# Revit family: Hager-Vega-IP30-syst-NoHosted-FR-fr
name_source: partatom
category: Electrical Equipment
units: mm (PartAtom-declared; Revit-internal decimal feet)

## family parameters
Always vertical = Yes
Cut with Voids When Loaded = No
Panel Configuration = Two Columns, Circuits Across
Part Type = Panelboard
Room Calculation Point = No
Round Connector Dimension = Use Diameter
Shared = No
Work Plane-Based = Yes

## types (8) — shared parameters
Default Elevation = 1219 mm
EF000003 - mode de pose = EV000384 - saillie
EF000007 - couleur = EV000202 - blanc
EF000008 - largeur = 400 mm  [stored 1.31234 ft]
EF000049 - profondeur = 146 mm  [stored 0.479003 ft]
EF000116 - numéro RAL = 9010
EF000118 - avec cadre/support de montage = No
EF000339 - type de capot = EV001012 - couvercle
EF001062 - finition CEM = No
EF001088 - possibilité de montage en saillie = Yes
EF001131 - profondeur intérieure = 120 mm
EF001134 - rail DIN = Yes
EF001596 - matériau du boîtier/corps = EV000139 - plastique
EF002950 - largeur en nombre de modules = 18
EF004462 - type de fermeture = EV000154 - autre
EF005474 - indice de protection (IP) = EV006410 - IP30
EF006244 - couvercle/porte transparent(e) = No
EF006306 - avec serrure = No
EF009212 - finition du couvercle = EV000116 - fermé
EF015776 - borne de mise à la terre = Yes
EF015777 - borne à conducteur neutre = No
EF015941 - porte pour transmission du signal = Yes
HG000001 - nombre de colonnes = 1
HG000002 - avec porte = No
HG000003 - Gamme = Vega
HG000005 - Epaisseur = 3 mm  [stored 0.00984252 ft]
HG000006 - Encastré = No
HG000009 - Porte à double battant = No
HG000010 - Portes asymétriques = No
HG000011 - Rangées du bas vides = No
HG000017 - Distance entre pôles = 18 mm  [stored 0.0590551 ft]
Manufacturer = Hager
Type Comments = Vega
zero-valued in all types: EF000218 - profondeur d'encastrement, EF000332 - hauteur d'encastrement, EF000846 - largeur d'encastrement, HG000007 - Nombre de colonnes vides, HG000008 - Nombre de rangées vides

## per-type parameters (varying)
| type | EF000040 - hauteur | EF000266 - nombre de rangées | HG000004 - Référence fabricant | Model |
| Saillie IP30 L400 H325 P146 18 Modules - VB118A | 325 mm | 1 | VB118A | VB118A |
| Saillie IP30 L400 H325 P146 18 Modules - VB118X | 325 mm | 1 | VB118X | VB118X |
| Saillie IP30 L400 H475 P146 18 Modules - VB218A | 475 mm  [stored 1.5584 ft] | 2 | VB218A | VB218A |
| Saillie IP30 L400 H475 P146 18 Modules - VB218X | 475 mm  [stored 1.5584 ft] | 2 | VB218X | VB218X |
| Saillie IP30 L400 H625 P146 18 Modules - VB318A | 625 mm  [stored 2.05052 ft] | 3 | VB318A | VB318A |
| Saillie IP30 L400 H625 P146 18 Modules - VB318X | 625 mm  [stored 2.05052 ft] | 3 | VB318X | VB318X |
| Saillie IP30 L400 H775 P146 18 Modules - VB418A | 775 mm  [stored 2.54265 ft] | 4 | VB418A | VB418A |
| Saillie IP30 L400 H775 P146 18 Modules - VB418X | 775 mm  [stored 2.54265 ft] | 4 | VB418X | VB418X |

note: [stored X ft] marks values corroborated as IEEE doubles in the binary element streams (Revit-internal decimal feet)

## geometry (parser evidence)
native form markers: Sweep x13
no freeform markers — native parametric forms only
